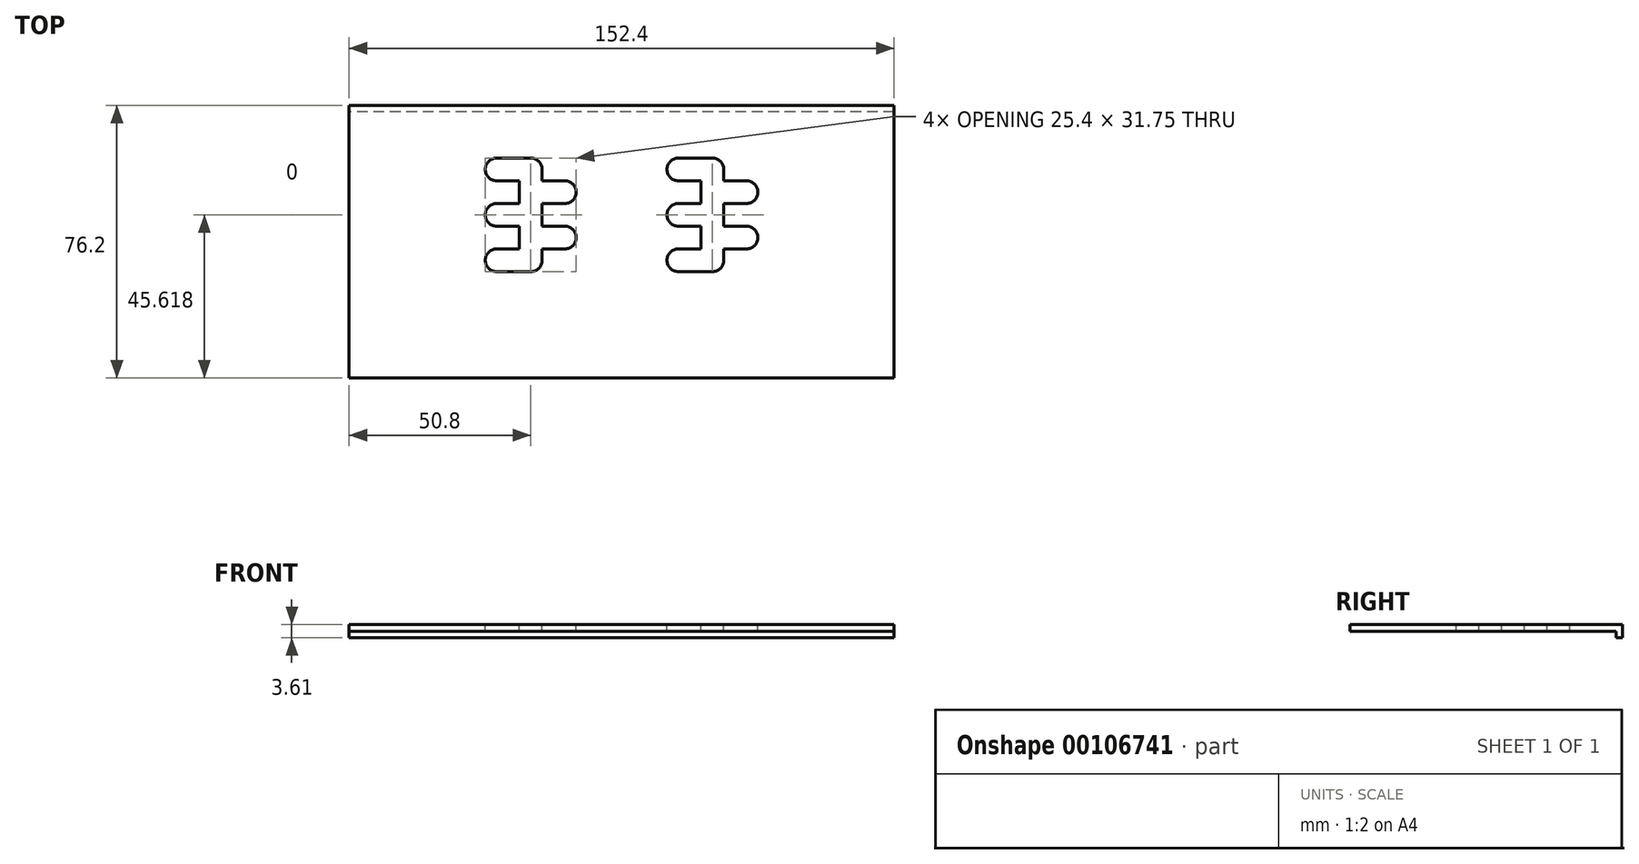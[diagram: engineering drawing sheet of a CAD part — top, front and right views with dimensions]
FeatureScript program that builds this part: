
annotation { "Feature Type Name" : "Feature", "Feature Type Description" : "" }
export const myFeature = defineFeature(function(context is Context, id is Id, definition is map)
    precondition{}
    {
        {
            var Q0;
            Q0=qCreatedBy(makeId("Right.planeOp"),FACE);
            var sketch = newSketch(context, id + "F0", { "sketchPlane" : qUnion([Q0])});
            skLineSegment(sketch, "E0.bottom", {"start": v(36.3, -0.9) * mm, "end": v(-38.1, -0.9) * mm});
            skLineSegment(sketch, "E0.top", {"start": v(38.1, 0.9) * mm, "end": v(-38.1, 0.9) * mm});
            skLineSegment(sketch, "E0.left", {"start": v(38.1, -0.9) * mm, "end": v(38.1, 0.9) * mm});
            skLineSegment(sketch, "E0.right", {"start": v(-38.1, -0.9) * mm, "end": v(-38.1, 0.9) * mm});
            skPoint(sketch, "E0.middle", {"position": v(0, 0) * mm});
            skLineSegment(sketch, "E1", {"start": v(38.1, -0.9) * mm, "end": v(38.1, -2.7) * mm});
            skLineSegment(sketch, "E2", {"start": v(38.1, -2.7) * mm, "end": v(36.3, -2.7) * mm});
            skLineSegment(sketch, "E3", {"start": v(36.3, -2.7) * mm, "end": v(36.3, -0.9) * mm});
            skSolve(sketch);
        }
        {
            var Q0;
            Q0=makeQuery(id+"F0.imprint","IMPRINT",FACE,{"disambiguationData":[TD([[makeQuery(id+"F0.imprint","IMPRINT",EDGE,{"derivedFrom":sQuery(id+"F0.wireOp",EDGE,"E0.bottom")}),-1.0]])]});
            extrude(context, id + "F1", {"entities" : qUnion([Q0]), "depth" : 76.2 * mm, "hasSecondDirection" : true, "secondDirectionOppositeDirection" : true, "secondDirectionDepth" : 76.2 * mm});
        }
        {
            var Q0;
            Q0=makeQuery(id+"F1.opExtrude","SWEPT_FACE",FACE,{"disambiguationData":[OSD([sQuery(id+"F0.wireOp",EDGE,"E0.top")])]});
            var sketch = newSketch(context, id + "F2", { "sketchPlane" : qUnion([Q0])});
            skLineSegment(sketch, "E4", {"start": v(0, 0) * mm, "end": v(-25.4, 0) * mm, "construction": true});
            skLineSegment(sketch, "E5", {"start": v(-38.1, 20.22) * mm, "end": v(-25.4, 20.22) * mm, "construction": true});
            skLineSegment(sketch, "E6", {"start": v(-25.4, 20.22) * mm, "end": v(-25.4, -5.18) * mm, "construction": true});
            skLineSegment(sketch, "E7", {"start": v(-38.1, -5.18) * mm, "end": v(-25.4, -5.18) * mm, "construction": true});
            skLineSegment(sketch, "E8", {"start": v(-25.4, 7.52) * mm, "end": v(-38.1, 7.52) * mm, "construction": true});
            skLineSegment(sketch, "E9", {"start": v(-25.4, 13.87) * mm, "end": v(-12.7, 13.87) * mm, "construction": true});
            skLineSegment(sketch, "E10", {"start": v(-25.4, 1.17) * mm, "end": v(-12.7, 1.17) * mm, "construction": true});
            skLineSegment(sketch, "E11", {"start": v(-38.1, 20.22) * mm, "end": v(-38.1, 20.22) * mm});
            skLineSegment(sketch, "E12", {"start": v(-34.93, 23.4) * mm, "end": v(-25.4, 23.4) * mm});
            skLineSegment(sketch, "E13", {"start": v(-12.7, 13.87) * mm, "end": v(-12.7, 13.87) * mm});
            skLineSegment(sketch, "E14", {"start": v(-22.23, 20.22) * mm, "end": v(-22.23, 17.04) * mm});
            skLineSegment(sketch, "E15", {"start": v(-15.88, 17.04) * mm, "end": v(-22.23, 17.04) * mm});
            skLineSegment(sketch, "E16", {"start": v(-15.88, 10.7) * mm, "end": v(-22.23, 10.7) * mm});
            skLineSegment(sketch, "E17", {"start": v(-22.23, 10.7) * mm, "end": v(-22.23, 4.34) * mm});
            skLineSegment(sketch, "E18", {"start": v(-12.7, 1.17) * mm, "end": v(-12.7, 1.17) * mm});
            skLineSegment(sketch, "E19", {"start": v(-15.88, 4.34) * mm, "end": v(-22.23, 4.34) * mm});
            skLineSegment(sketch, "E20", {"start": v(-15.88, -2) * mm, "end": v(-22.23, -2) * mm});
            skLineSegment(sketch, "E21", {"start": v(-22.23, -2) * mm, "end": v(-22.23, -5.18) * mm});
            skLineSegment(sketch, "E22", {"start": v(-25.4, -8.36) * mm, "end": v(-34.93, -8.36) * mm});
            skLineSegment(sketch, "E23", {"start": v(-38.1, -5.18) * mm, "end": v(-38.1, -5.18) * mm});
            skLineSegment(sketch, "E24", {"start": v(-34.93, -2) * mm, "end": v(-28.58, -2) * mm});
            skLineSegment(sketch, "E25", {"start": v(-28.58, -2) * mm, "end": v(-28.58, 4.34) * mm});
            skLineSegment(sketch, "E26", {"start": v(-28.58, 4.34) * mm, "end": v(-34.93, 4.34) * mm});
            skLineSegment(sketch, "E27", {"start": v(-38.1, 7.52) * mm, "end": v(-38.1, 7.52) * mm});
            skLineSegment(sketch, "E28", {"start": v(-34.93, 17.04) * mm, "end": v(-28.58, 17.04) * mm});
            skLineSegment(sketch, "E29", {"start": v(-28.58, 17.04) * mm, "end": v(-28.58, 10.7) * mm});
            skLineSegment(sketch, "E30", {"start": v(-28.58, 10.7) * mm, "end": v(-34.93, 10.7) * mm});
            skPoint(sketch, "E31.visualSharp", {"position": v(-38.1, 23.4) * mm});
            skArc(sketch, "E31.filletArc", {"start": v(-34.93, 23.4) * mm, "mid": v(-37.17, 22.46) * mm, "end": v(-38.1, 20.22) * mm});
            skPoint(sketch, "E32.visualSharp", {"position": v(-38.1, 17.04) * mm});
            skArc(sketch, "E32.filletArc", {"start": v(-38.1, 20.22) * mm, "mid": v(-37.17, 17.97) * mm, "end": v(-34.93, 17.04) * mm});
            skPoint(sketch, "E33.visualSharp", {"position": v(-22.23, 23.4) * mm});
            skArc(sketch, "E33.filletArc", {"start": v(-22.23, 20.22) * mm, "mid": v(-23.15, 22.46) * mm, "end": v(-25.4, 23.4) * mm});
            skPoint(sketch, "E34.visualSharp", {"position": v(-38.1, 10.7) * mm});
            skArc(sketch, "E34.filletArc", {"start": v(-34.93, 10.7) * mm, "mid": v(-37.17, 9.76) * mm, "end": v(-38.1, 7.52) * mm});
            skPoint(sketch, "E35.visualSharp", {"position": v(-38.1, 4.34) * mm});
            skArc(sketch, "E35.filletArc", {"start": v(-38.1, 7.52) * mm, "mid": v(-37.17, 5.27) * mm, "end": v(-34.93, 4.34) * mm});
            skPoint(sketch, "E36.visualSharp", {"position": v(-12.7, 17.04) * mm});
            skArc(sketch, "E36.filletArc", {"start": v(-12.7, 13.87) * mm, "mid": v(-13.63, 16.11) * mm, "end": v(-15.88, 17.04) * mm});
            skPoint(sketch, "E37.visualSharp", {"position": v(-12.7, 10.7) * mm});
            skArc(sketch, "E37.filletArc", {"start": v(-15.88, 10.7) * mm, "mid": v(-13.63, 11.62) * mm, "end": v(-12.7, 13.87) * mm});
            skPoint(sketch, "E38.visualSharp", {"position": v(-12.7, 4.34) * mm});
            skArc(sketch, "E38.filletArc", {"start": v(-12.7, 1.17) * mm, "mid": v(-13.63, 3.41) * mm, "end": v(-15.88, 4.34) * mm});
            skPoint(sketch, "E39.visualSharp", {"position": v(-12.7, -2) * mm});
            skArc(sketch, "E39.filletArc", {"start": v(-15.88, -2) * mm, "mid": v(-13.63, -1.08) * mm, "end": v(-12.7, 1.17) * mm});
            skPoint(sketch, "E40.visualSharp", {"position": v(-22.23, -8.36) * mm});
            skArc(sketch, "E40.filletArc", {"start": v(-25.4, -8.36) * mm, "mid": v(-23.15, -7.43) * mm, "end": v(-22.23, -5.18) * mm});
            skPoint(sketch, "E41.visualSharp", {"position": v(-38.1, -2) * mm});
            skArc(sketch, "E41.filletArc", {"start": v(-34.93, -2) * mm, "mid": v(-37.17, -2.94) * mm, "end": v(-38.1, -5.18) * mm});
            skPoint(sketch, "E42.visualSharp", {"position": v(-38.1, -8.36) * mm});
            skArc(sketch, "E42.filletArc", {"start": v(-38.1, -5.18) * mm, "mid": v(-37.17, -7.43) * mm, "end": v(-34.93, -8.36) * mm});
            skSolve(sketch);
        }
        {
            var Q0;
            Q0 = qSketchRegion(id + "F2", true);
            extrude(context, id + "F3", {"entities" : qUnion([Q0]), "operationType" : NewBodyOperationType.REMOVE, "endBound" : BoundingType.THROUGH_ALL, "oppositeDirection" : true, "depth" : 25.4 * mm});
        }
        {
            var Q0;
            Q0=makeQuery(id+"F1.opExtrude","SWEPT_FACE",FACE,{"disambiguationData":[OSD([sQuery(id+"F0.wireOp",EDGE,"E0.top")])]});
            var sketch = newSketch(context, id + "F4", { "sketchPlane" : qUnion([Q0])});
            skLineSegment(sketch, "E43", {"start": v(55.32, 0.86) * mm, "end": v(29.92, 0.86) * mm, "construction": true});
            skLineSegment(sketch, "E44", {"start": v(12.7, 20.22) * mm, "end": v(25.4, 20.22) * mm, "construction": true});
            skLineSegment(sketch, "E45", {"start": v(25.4, 20.22) * mm, "end": v(25.4, -5.18) * mm, "construction": true});
            skLineSegment(sketch, "E46", {"start": v(12.7, -5.18) * mm, "end": v(25.4, -5.18) * mm, "construction": true});
            skLineSegment(sketch, "E47", {"start": v(25.4, 7.52) * mm, "end": v(12.7, 7.52) * mm, "construction": true});
            skLineSegment(sketch, "E48", {"start": v(25.4, 13.87) * mm, "end": v(38.1, 13.87) * mm, "construction": true});
            skLineSegment(sketch, "E49", {"start": v(25.4, 1.17) * mm, "end": v(38.1, 1.17) * mm, "construction": true});
            skLineSegment(sketch, "E50", {"start": v(12.7, 20.22) * mm, "end": v(12.7, 20.22) * mm});
            skLineSegment(sketch, "E51", {"start": v(15.88, 23.4) * mm, "end": v(25.4, 23.4) * mm});
            skLineSegment(sketch, "E52", {"start": v(38.1, 13.87) * mm, "end": v(38.1, 13.87) * mm});
            skLineSegment(sketch, "E53", {"start": v(28.58, 20.22) * mm, "end": v(28.58, 17.04) * mm});
            skLineSegment(sketch, "E54", {"start": v(34.93, 17.04) * mm, "end": v(28.58, 17.04) * mm});
            skLineSegment(sketch, "E55", {"start": v(34.93, 10.7) * mm, "end": v(28.58, 10.7) * mm});
            skLineSegment(sketch, "E56", {"start": v(28.58, 10.7) * mm, "end": v(28.58, 4.34) * mm});
            skLineSegment(sketch, "E57", {"start": v(38.1, 1.17) * mm, "end": v(38.1, 1.17) * mm});
            skLineSegment(sketch, "E58", {"start": v(34.93, 4.34) * mm, "end": v(28.58, 4.34) * mm});
            skLineSegment(sketch, "E59", {"start": v(34.93, -2) * mm, "end": v(28.58, -2) * mm});
            skLineSegment(sketch, "E60", {"start": v(28.58, -2) * mm, "end": v(28.58, -5.18) * mm});
            skLineSegment(sketch, "E61", {"start": v(25.4, -8.36) * mm, "end": v(15.88, -8.36) * mm});
            skLineSegment(sketch, "E62", {"start": v(12.7, -5.18) * mm, "end": v(12.7, -5.18) * mm});
            skLineSegment(sketch, "E63", {"start": v(15.88, -2) * mm, "end": v(22.23, -2) * mm});
            skLineSegment(sketch, "E64", {"start": v(22.23, -2) * mm, "end": v(22.23, 4.34) * mm});
            skLineSegment(sketch, "E65", {"start": v(22.23, 4.34) * mm, "end": v(15.88, 4.34) * mm});
            skLineSegment(sketch, "E66", {"start": v(12.7, 7.52) * mm, "end": v(12.7, 7.52) * mm});
            skLineSegment(sketch, "E67", {"start": v(15.88, 17.04) * mm, "end": v(22.23, 17.04) * mm});
            skLineSegment(sketch, "E68", {"start": v(22.23, 17.04) * mm, "end": v(22.23, 10.7) * mm});
            skLineSegment(sketch, "E69", {"start": v(22.23, 10.7) * mm, "end": v(15.88, 10.7) * mm});
            skPoint(sketch, "E70.visualSharp", {"position": v(12.7, 23.4) * mm});
            skArc(sketch, "E70.filletArc", {"start": v(15.88, 23.4) * mm, "mid": v(13.63, 22.46) * mm, "end": v(12.7, 20.22) * mm});
            skPoint(sketch, "E71.visualSharp", {"position": v(28.58, 23.4) * mm});
            skArc(sketch, "E71.filletArc", {"start": v(28.58, 20.22) * mm, "mid": v(27.65, 22.46) * mm, "end": v(25.4, 23.4) * mm});
            skPoint(sketch, "E72.visualSharp", {"position": v(12.7, 17.04) * mm});
            skArc(sketch, "E72.filletArc", {"start": v(12.7, 20.22) * mm, "mid": v(13.63, 17.97) * mm, "end": v(15.88, 17.04) * mm});
            skPoint(sketch, "E73.visualSharp", {"position": v(38.1, 17.04) * mm});
            skArc(sketch, "E73.filletArc", {"start": v(38.1, 13.87) * mm, "mid": v(37.17, 16.11) * mm, "end": v(34.93, 17.04) * mm});
            skPoint(sketch, "E74.visualSharp", {"position": v(38.1, 10.7) * mm});
            skArc(sketch, "E74.filletArc", {"start": v(34.93, 10.7) * mm, "mid": v(37.17, 11.62) * mm, "end": v(38.1, 13.87) * mm});
            skPoint(sketch, "E75.visualSharp", {"position": v(12.7, 10.7) * mm});
            skArc(sketch, "E75.filletArc", {"start": v(15.88, 10.7) * mm, "mid": v(13.63, 9.76) * mm, "end": v(12.7, 7.52) * mm});
            skPoint(sketch, "E76.visualSharp", {"position": v(12.7, 4.34) * mm});
            skArc(sketch, "E76.filletArc", {"start": v(12.7, 7.52) * mm, "mid": v(13.63, 5.27) * mm, "end": v(15.88, 4.34) * mm});
            skPoint(sketch, "E77.visualSharp", {"position": v(38.1, 4.34) * mm});
            skArc(sketch, "E77.filletArc", {"start": v(38.1, 1.17) * mm, "mid": v(37.17, 3.41) * mm, "end": v(34.93, 4.34) * mm});
            skPoint(sketch, "E78.visualSharp", {"position": v(38.1, -2) * mm});
            skArc(sketch, "E78.filletArc", {"start": v(34.93, -2) * mm, "mid": v(37.17, -1.08) * mm, "end": v(38.1, 1.17) * mm});
            skPoint(sketch, "E79.visualSharp", {"position": v(12.7, -2) * mm});
            skArc(sketch, "E79.filletArc", {"start": v(15.88, -2) * mm, "mid": v(13.63, -2.94) * mm, "end": v(12.7, -5.18) * mm});
            skPoint(sketch, "E80.visualSharp", {"position": v(12.7, -8.36) * mm});
            skArc(sketch, "E80.filletArc", {"start": v(12.7, -5.18) * mm, "mid": v(13.63, -7.43) * mm, "end": v(15.88, -8.36) * mm});
            skPoint(sketch, "E81.visualSharp", {"position": v(28.58, -8.36) * mm});
            skArc(sketch, "E81.filletArc", {"start": v(25.4, -8.36) * mm, "mid": v(27.65, -7.43) * mm, "end": v(28.58, -5.18) * mm});
            skSolve(sketch);
        }
        {
            var Q0;
            Q0 = qSketchRegion(id + "F4", true);
            extrude(context, id + "F5", {"entities" : qUnion([Q0]), "operationType" : NewBodyOperationType.REMOVE, "endBound" : BoundingType.THROUGH_ALL, "oppositeDirection" : true, "depth" : 25.4 * mm});
        }
        {
            var Q0;
            Q0=makeQuery(id+"F1.opExtrude","SWEPT_BODY",BODY,{"disambiguationData":[OSD([sQuery(id+"F0.wireOp",EDGE,"E0.bottom"),sQuery(id+"F0.wireOp",EDGE,"E0.top"),sQuery(id+"F0.wireOp",EDGE,"E0.left"),sQuery(id+"F0.wireOp",EDGE,"E0.right"),sQuery(id+"F0.wireOp",EDGE,"E1"),sQuery(id+"F0.wireOp",EDGE,"E2"),sQuery(id+"F0.wireOp",EDGE,"E3")])]});
            transform(context, id + "F6", {"entities" : qUnion([Q0]), "transformType" : TransformType.TRANSLATION_3D, "dx" : 0 * mm, "dy" : 0 * mm, "dz" : 0 * mm, "makeCopy" : true});
        }
    });
